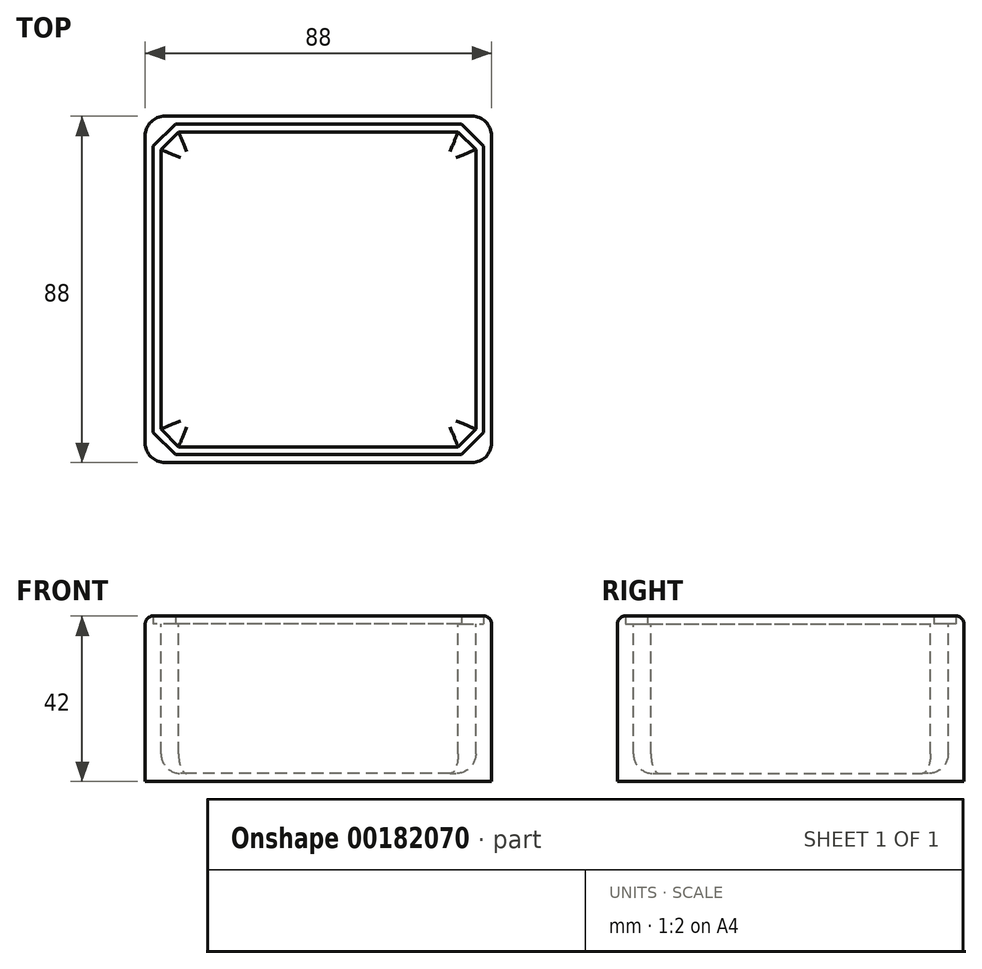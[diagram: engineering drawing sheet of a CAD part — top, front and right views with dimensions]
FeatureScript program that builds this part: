
annotation { "Feature Type Name" : "Feature", "Feature Type Description" : "" }
export const myFeature = defineFeature(function(context is Context, id is Id, definition is map)
    precondition{}
    {
        {
            var Q0;
            Q0=qCreatedBy(makeId("Top.planeOp"),FACE);
            var sketch = newSketch(context, id + "F0", { "sketchPlane" : qUnion([Q0])});
            skLineSegment(sketch, "E0.bottom", {"start": v(42, -42) * mm, "end": v(-42, -42) * mm});
            skLineSegment(sketch, "E0.top", {"start": v(42, 42) * mm, "end": v(-42, 42) * mm});
            skLineSegment(sketch, "E0.left", {"start": v(42, -42) * mm, "end": v(42, 42) * mm});
            skLineSegment(sketch, "E0.right", {"start": v(-42, -42) * mm, "end": v(-42, 42) * mm});
            skPoint(sketch, "E0.middle", {"position": v(0, 0) * mm});
            skLineSegment(sketch, "E1", {"start": v(-36.34, 42) * mm, "end": v(-42, 36.34) * mm});
            skLineSegment(sketch, "E2.MirrorCS", {"start": v(-36.34, -42) * mm, "end": v(-42, -36.34) * mm});
            skLineSegment(sketch, "E3.MirrorCS", {"start": v(36.34, 42) * mm, "end": v(42, 36.34) * mm});
            skLineSegment(sketch, "E4.MirrorCS", {"start": v(36.34, -42) * mm, "end": v(42, -36.34) * mm});
            skLineSegment(sketch, "E5.bottom", {"start": v(39, -44) * mm, "end": v(-39, -44) * mm});
            skLineSegment(sketch, "E5.top", {"start": v(39, 44) * mm, "end": v(-39, 44) * mm});
            skLineSegment(sketch, "E5.left", {"start": v(44, -39) * mm, "end": v(44, 39) * mm});
            skLineSegment(sketch, "E5.right", {"start": v(-44, -39) * mm, "end": v(-44, 39) * mm});
            skPoint(sketch, "E6.visualSharp", {"position": v(44, 44) * mm});
            skArc(sketch, "E6.filletArc", {"start": v(44, 39) * mm, "mid": v(42.54, 42.54) * mm, "end": v(39, 44) * mm});
            skPoint(sketch, "E7.visualSharp", {"position": v(-44, 44) * mm});
            skArc(sketch, "E7.filletArc", {"start": v(-39, 44) * mm, "mid": v(-42.54, 42.54) * mm, "end": v(-44, 39) * mm});
            skPoint(sketch, "E8.visualSharp", {"position": v(-44, -44) * mm});
            skArc(sketch, "E8.filletArc", {"start": v(-44, -39) * mm, "mid": v(-42.54, -42.54) * mm, "end": v(-39, -44) * mm});
            skPoint(sketch, "E9.visualSharp", {"position": v(44, -44) * mm});
            skArc(sketch, "E9.filletArc", {"start": v(39, -44) * mm, "mid": v(42.54, -42.54) * mm, "end": v(44, -39) * mm});
            skLineSegment(sketch, "E10.0", {"start": v(40, 40) * mm, "end": v(-40, 40) * mm});
            skLineSegment(sketch, "E10.1", {"start": v(40, -40) * mm, "end": v(40, 40) * mm});
            skLineSegment(sketch, "E10.2", {"start": v(40, -40) * mm, "end": v(-40, -40) * mm});
            skLineSegment(sketch, "E10.3", {"start": v(-40, -40) * mm, "end": v(-40, 40) * mm});
            skLineSegment(sketch, "E11.0", {"start": v(-35.51, 40) * mm, "end": v(-40, 35.51) * mm});
            skLineSegment(sketch, "E12.0", {"start": v(35.51, 40) * mm, "end": v(40, 35.51) * mm});
            skLineSegment(sketch, "E13.0", {"start": v(35.51, -40) * mm, "end": v(40, -35.51) * mm});
            skLineSegment(sketch, "E14.0", {"start": v(-35.51, -40) * mm, "end": v(-40, -35.51) * mm});
            skSolve(sketch);
        }
        {
            var Q0;
            Q0=makeQuery(id+"F0.imprint","IMPRINT",FACE,{"disambiguationData":[TD([[makeQuery(id+"F0.imprint","IMPRINT",EDGE,{"derivedFrom":sQuery(id+"F0.wireOp",EDGE,"E5.bottom")}),-1.0]])]});
            var Q1;
            {var subQ5=sQuery(id+"F0.wireOp",EDGE,"E11.0");Q1=makeQuery(id+"F0.imprint","IMPRINT",FACE,{"disambiguationData":[TD([[makeQuery(id+"F0.imprint","IMPRINT",EDGE,{"derivedFrom":subQ5}),1.0]])]});}
            var Q2;
            {var subQ5=sQuery(id+"F0.wireOp",EDGE,"E12.0");Q2=makeQuery(id+"F0.imprint","IMPRINT",FACE,{"disambiguationData":[TD([[makeQuery(id+"F0.imprint","IMPRINT",EDGE,{"derivedFrom":subQ5}),1.0]])]});}
            var Q3;
            {var subQ1=sQuery(id+"F0.wireOp",EDGE,"E0.left");var subQ5=sQuery(id+"F0.wireOp",EDGE,"E0.top");var subQ6=makeQuery(id+"F0.imprint","INTERSECT",VERTEX,{"derivedFrom":[subQ5,subQ1]});Q3=makeQuery(id+"F0.imprint","IMPRINT",FACE,{"disambiguationData":[TD([[makeQuery(id+"F0.imprint","IMPRINT",EDGE,{"disambiguationData":[TD([[subQ6,-1.0]])],"derivedFrom":subQ5}),1.0]])]});}
            var Q4;
            {var subQ0=sQuery(id+"F0.wireOp",EDGE,"E10.0");var subQ1=sQuery(id+"F0.wireOp",EDGE,"E3.MirrorCS");var subQ2=makeQuery(id+"F0.imprint","INTERSECT",VERTEX,{"derivedFrom":[subQ1,subQ0]});Q4=makeQuery(id+"F0.imprint","IMPRINT",FACE,{"disambiguationData":[TD([[makeQuery(id+"F0.imprint","IMPRINT",EDGE,{"disambiguationData":[TD([[subQ2,-1.0]])],"derivedFrom":subQ1}),1.0]])]});}
            var Q5;
            {var subQ4=sQuery(id+"F0.wireOp",EDGE,"E0.left");var subQ7=sQuery(id+"F0.wireOp",EDGE,"E3.MirrorCS");var subQ9=makeQuery(id+"F0.imprint","INTERSECT",VERTEX,{"derivedFrom":[subQ4,subQ7]});Q5=makeQuery(id+"F0.imprint","IMPRINT",FACE,{"disambiguationData":[TD([[makeQuery(id+"F0.imprint","IMPRINT",EDGE,{"disambiguationData":[TD([[subQ9,1.0]])],"derivedFrom":subQ4}),1.0]])]});}
            var Q6;
            {var subQ4=sQuery(id+"F0.wireOp",EDGE,"E0.top");var subQ6=sQuery(id+"F0.wireOp",EDGE,"E1");var subQ7=makeQuery(id+"F0.imprint","INTERSECT",VERTEX,{"derivedFrom":[subQ4,subQ6]});Q6=makeQuery(id+"F0.imprint","IMPRINT",FACE,{"disambiguationData":[TD([[makeQuery(id+"F0.imprint","IMPRINT",EDGE,{"disambiguationData":[TD([[subQ7,1.0]])],"derivedFrom":subQ4}),1.0]])]});}
            var Q7;
            {var subQ5=sQuery(id+"F0.wireOp",EDGE,"E11.0");Q7=makeQuery(id+"F0.imprint","IMPRINT",FACE,{"disambiguationData":[TD([[makeQuery(id+"F0.imprint","IMPRINT",EDGE,{"derivedFrom":subQ5}),-1.0]])]});}
            var Q8;
            {var subQ0=sQuery(id+"F0.wireOp",EDGE,"E10.0");var subQ1=sQuery(id+"F0.wireOp",EDGE,"E1");var subQ2=makeQuery(id+"F0.imprint","INTERSECT",VERTEX,{"derivedFrom":[subQ1,subQ0]});Q8=makeQuery(id+"F0.imprint","IMPRINT",FACE,{"disambiguationData":[TD([[makeQuery(id+"F0.imprint","IMPRINT",EDGE,{"disambiguationData":[TD([[subQ2,-1.0]])],"derivedFrom":subQ1}),-1.0]])]});}
            var Q9;
            {var subQ1=sQuery(id+"F0.wireOp",EDGE,"E0.right");var subQ5=sQuery(id+"F0.wireOp",EDGE,"E0.top");var subQ9=makeQuery(id+"F0.imprint","INTERSECT",VERTEX,{"derivedFrom":[subQ5,subQ1]});Q9=makeQuery(id+"F0.imprint","IMPRINT",FACE,{"disambiguationData":[TD([[makeQuery(id+"F0.imprint","IMPRINT",EDGE,{"disambiguationData":[TD([[subQ9,1.0]])],"derivedFrom":subQ5}),1.0]])]});}
            var Q10;
            {var subQ4=sQuery(id+"F0.wireOp",EDGE,"E0.right");var subQ6=sQuery(id+"F0.wireOp",EDGE,"E1");var subQ7=makeQuery(id+"F0.imprint","INTERSECT",VERTEX,{"derivedFrom":[subQ4,subQ6]});Q10=makeQuery(id+"F0.imprint","IMPRINT",FACE,{"disambiguationData":[TD([[makeQuery(id+"F0.imprint","IMPRINT",EDGE,{"disambiguationData":[TD([[subQ7,1.0]])],"derivedFrom":subQ4}),-1.0]])]});}
            var Q11;
            {var subQ5=sQuery(id+"F0.wireOp",EDGE,"E14.0");Q11=makeQuery(id+"F0.imprint","IMPRINT",FACE,{"disambiguationData":[TD([[makeQuery(id+"F0.imprint","IMPRINT",EDGE,{"derivedFrom":subQ5}),1.0]])]});}
            var Q12;
            {var subQ0=sQuery(id+"F0.wireOp",EDGE,"E10.2");var subQ1=sQuery(id+"F0.wireOp",EDGE,"E2.MirrorCS");var subQ2=makeQuery(id+"F0.imprint","INTERSECT",VERTEX,{"derivedFrom":[subQ1,subQ0]});Q12=makeQuery(id+"F0.imprint","IMPRINT",FACE,{"disambiguationData":[TD([[makeQuery(id+"F0.imprint","IMPRINT",EDGE,{"disambiguationData":[TD([[subQ2,-1.0]])],"derivedFrom":subQ1}),1.0]])]});}
            var Q13;
            {var subQ1=sQuery(id+"F0.wireOp",EDGE,"E0.bottom");var subQ5=sQuery(id+"F0.wireOp",EDGE,"E0.right");var subQ6=makeQuery(id+"F0.imprint","INTERSECT",VERTEX,{"derivedFrom":[subQ1,subQ5]});Q13=makeQuery(id+"F0.imprint","IMPRINT",FACE,{"disambiguationData":[TD([[makeQuery(id+"F0.imprint","IMPRINT",EDGE,{"disambiguationData":[TD([[subQ6,1.0]])],"derivedFrom":subQ1}),-1.0]])]});}
            var Q14;
            {var subQ1=sQuery(id+"F0.wireOp",EDGE,"E0.bottom");var subQ5=sQuery(id+"F0.wireOp",EDGE,"E2.MirrorCS");var subQ6=makeQuery(id+"F0.imprint","INTERSECT",VERTEX,{"derivedFrom":[subQ1,subQ5]});Q14=makeQuery(id+"F0.imprint","IMPRINT",FACE,{"disambiguationData":[TD([[makeQuery(id+"F0.imprint","IMPRINT",EDGE,{"disambiguationData":[TD([[subQ6,1.0]])],"derivedFrom":subQ1}),-1.0]])]});}
            var Q15;
            {var subQ5=sQuery(id+"F0.wireOp",EDGE,"E13.0");Q15=makeQuery(id+"F0.imprint","IMPRINT",FACE,{"disambiguationData":[TD([[makeQuery(id+"F0.imprint","IMPRINT",EDGE,{"derivedFrom":subQ5}),-1.0]])]});}
            var Q16;
            {var subQ0=sQuery(id+"F0.wireOp",EDGE,"E10.2");var subQ1=sQuery(id+"F0.wireOp",EDGE,"E4.MirrorCS");var subQ2=makeQuery(id+"F0.imprint","INTERSECT",VERTEX,{"derivedFrom":[subQ1,subQ0]});Q16=makeQuery(id+"F0.imprint","IMPRINT",FACE,{"disambiguationData":[TD([[makeQuery(id+"F0.imprint","IMPRINT",EDGE,{"disambiguationData":[TD([[subQ2,-1.0]])],"derivedFrom":subQ1}),-1.0]])]});}
            var Q17;
            {var subQ1=sQuery(id+"F0.wireOp",EDGE,"E0.bottom");var subQ5=sQuery(id+"F0.wireOp",EDGE,"E0.left");var subQ6=makeQuery(id+"F0.imprint","INTERSECT",VERTEX,{"derivedFrom":[subQ1,subQ5]});Q17=makeQuery(id+"F0.imprint","IMPRINT",FACE,{"disambiguationData":[TD([[makeQuery(id+"F0.imprint","IMPRINT",EDGE,{"disambiguationData":[TD([[subQ6,-1.0]])],"derivedFrom":subQ1}),-1.0]])]});}
            extrude(context, id + "F1", {"entities" : qUnion([Q0, Q1, Q2, Q3, Q4, Q5, Q6, Q7, Q8, Q9, Q10, Q11, Q12, Q13, Q14, Q15, Q16, Q17]), "oppositeDirection" : true, "depth" : 40 * mm});
        }
        {
            var Q0;
            {var subQ5=sQuery(id+"F0.wireOp",EDGE,"E11.0");Q0=makeQuery(id+"F0.imprint","IMPRINT",FACE,{"disambiguationData":[TD([[makeQuery(id+"F0.imprint","IMPRINT",EDGE,{"derivedFrom":subQ5}),1.0]])]});}
            extrude(context, id + "F2", {"entities" : qUnion([Q0]), "operationType" : NewBodyOperationType.REMOVE, "oppositeDirection" : true, "depth" : 38 * mm});
        }
        {
            var Q0;
            Q0=makeQuery(id+"F0.imprint","IMPRINT",FACE,{"disambiguationData":[TD([[makeQuery(id+"F0.imprint","IMPRINT",EDGE,{"derivedFrom":sQuery(id+"F0.wireOp",EDGE,"E5.bottom")}),-1.0]])]});
            var Q1;
            {var subQ1=sQuery(id+"F0.wireOp",EDGE,"E0.right");var subQ5=sQuery(id+"F0.wireOp",EDGE,"E0.top");var subQ9=makeQuery(id+"F0.imprint","INTERSECT",VERTEX,{"derivedFrom":[subQ5,subQ1]});Q1=makeQuery(id+"F0.imprint","IMPRINT",FACE,{"disambiguationData":[TD([[makeQuery(id+"F0.imprint","IMPRINT",EDGE,{"disambiguationData":[TD([[subQ9,1.0]])],"derivedFrom":subQ5}),1.0]])]});}
            var Q2;
            {var subQ0=sQuery(id+"F0.wireOp",EDGE,"E10.0");var subQ1=sQuery(id+"F0.wireOp",EDGE,"E1");var subQ2=makeQuery(id+"F0.imprint","INTERSECT",VERTEX,{"derivedFrom":[subQ1,subQ0]});Q2=makeQuery(id+"F0.imprint","IMPRINT",FACE,{"disambiguationData":[TD([[makeQuery(id+"F0.imprint","IMPRINT",EDGE,{"disambiguationData":[TD([[subQ2,-1.0]])],"derivedFrom":subQ1}),-1.0]])]});}
            var Q3;
            {var subQ1=sQuery(id+"F0.wireOp",EDGE,"E0.left");var subQ5=sQuery(id+"F0.wireOp",EDGE,"E0.top");var subQ6=makeQuery(id+"F0.imprint","INTERSECT",VERTEX,{"derivedFrom":[subQ5,subQ1]});Q3=makeQuery(id+"F0.imprint","IMPRINT",FACE,{"disambiguationData":[TD([[makeQuery(id+"F0.imprint","IMPRINT",EDGE,{"disambiguationData":[TD([[subQ6,-1.0]])],"derivedFrom":subQ5}),1.0]])]});}
            var Q4;
            {var subQ0=sQuery(id+"F0.wireOp",EDGE,"E10.0");var subQ1=sQuery(id+"F0.wireOp",EDGE,"E3.MirrorCS");var subQ2=makeQuery(id+"F0.imprint","INTERSECT",VERTEX,{"derivedFrom":[subQ1,subQ0]});Q4=makeQuery(id+"F0.imprint","IMPRINT",FACE,{"disambiguationData":[TD([[makeQuery(id+"F0.imprint","IMPRINT",EDGE,{"disambiguationData":[TD([[subQ2,-1.0]])],"derivedFrom":subQ1}),1.0]])]});}
            var Q5;
            {var subQ1=sQuery(id+"F0.wireOp",EDGE,"E0.bottom");var subQ5=sQuery(id+"F0.wireOp",EDGE,"E0.left");var subQ6=makeQuery(id+"F0.imprint","INTERSECT",VERTEX,{"derivedFrom":[subQ1,subQ5]});Q5=makeQuery(id+"F0.imprint","IMPRINT",FACE,{"disambiguationData":[TD([[makeQuery(id+"F0.imprint","IMPRINT",EDGE,{"disambiguationData":[TD([[subQ6,-1.0]])],"derivedFrom":subQ1}),-1.0]])]});}
            var Q6;
            {var subQ0=sQuery(id+"F0.wireOp",EDGE,"E10.2");var subQ1=sQuery(id+"F0.wireOp",EDGE,"E4.MirrorCS");var subQ2=makeQuery(id+"F0.imprint","INTERSECT",VERTEX,{"derivedFrom":[subQ1,subQ0]});Q6=makeQuery(id+"F0.imprint","IMPRINT",FACE,{"disambiguationData":[TD([[makeQuery(id+"F0.imprint","IMPRINT",EDGE,{"disambiguationData":[TD([[subQ2,-1.0]])],"derivedFrom":subQ1}),-1.0]])]});}
            var Q7;
            {var subQ1=sQuery(id+"F0.wireOp",EDGE,"E0.bottom");var subQ5=sQuery(id+"F0.wireOp",EDGE,"E0.right");var subQ6=makeQuery(id+"F0.imprint","INTERSECT",VERTEX,{"derivedFrom":[subQ1,subQ5]});Q7=makeQuery(id+"F0.imprint","IMPRINT",FACE,{"disambiguationData":[TD([[makeQuery(id+"F0.imprint","IMPRINT",EDGE,{"disambiguationData":[TD([[subQ6,1.0]])],"derivedFrom":subQ1}),-1.0]])]});}
            var Q8;
            {var subQ0=sQuery(id+"F0.wireOp",EDGE,"E10.2");var subQ1=sQuery(id+"F0.wireOp",EDGE,"E2.MirrorCS");var subQ2=makeQuery(id+"F0.imprint","INTERSECT",VERTEX,{"derivedFrom":[subQ1,subQ0]});Q8=makeQuery(id+"F0.imprint","IMPRINT",FACE,{"disambiguationData":[TD([[makeQuery(id+"F0.imprint","IMPRINT",EDGE,{"disambiguationData":[TD([[subQ2,-1.0]])],"derivedFrom":subQ1}),1.0]])]});}
            extrude(context, id + "F3", {"entities" : qUnion([Q0, Q1, Q2, Q3, Q4, Q5, Q6, Q7, Q8]), "operationType" : NewBodyOperationType.ADD, "depth" : 2 * mm});
        }
        {
            var Q0;
            Q0=makeQuery(id+"F3.opExtrude","CAP_EDGE",EDGE,{"disambiguationData":[OSD([sQuery(id+"F0.wireOp",EDGE,"E8.filletArc")])],"isStart":false});
            fillet(context, id + "F4", {"entities" : qUnion([Q0]), "radius" : 2 * mm, "tangentPropagation" : true, "allowEdgeOverflow" : false});
        }
        {
            var Q0;
            Q0=makeQuery(id+"F2.boolean.opBoolean","COPY",EDGE,{"derivedFrom":makeQuery(id+"F2.opExtrude","CAP_EDGE",EDGE,{"disambiguationData":[OSD([sQuery(id+"F0.wireOp",EDGE,"E10.0")])],"isStart":false})});
            var Q1;
            Q1=makeQuery(id+"F2.boolean.opBoolean","COPY",EDGE,{"derivedFrom":makeQuery(id+"F2.opExtrude","CAP_EDGE",EDGE,{"disambiguationData":[OSD([sQuery(id+"F0.wireOp",EDGE,"E10.3")])],"isStart":false})});
            var Q2;
            Q2=makeQuery(id+"F2.boolean.opBoolean","COPY",EDGE,{"derivedFrom":makeQuery(id+"F2.opExtrude","CAP_EDGE",EDGE,{"disambiguationData":[OSD([sQuery(id+"F0.wireOp",EDGE,"E11.0")])],"isStart":false})});
            var Q3;
            Q3=makeQuery(id+"F2.boolean.opBoolean","COPY",EDGE,{"derivedFrom":makeQuery(id+"F2.opExtrude","CAP_EDGE",EDGE,{"disambiguationData":[OSD([sQuery(id+"F0.wireOp",EDGE,"E14.0")])],"isStart":false})});
            var Q4;
            Q4=makeQuery(id+"F2.boolean.opBoolean","COPY",EDGE,{"derivedFrom":makeQuery(id+"F2.opExtrude","CAP_EDGE",EDGE,{"disambiguationData":[OSD([sQuery(id+"F0.wireOp",EDGE,"E10.2")])],"isStart":false})});
            var Q5;
            Q5=makeQuery(id+"F2.boolean.opBoolean","COPY",EDGE,{"derivedFrom":makeQuery(id+"F2.opExtrude","CAP_EDGE",EDGE,{"disambiguationData":[OSD([sQuery(id+"F0.wireOp",EDGE,"E13.0")])],"isStart":false})});
            var Q6;
            Q6=makeQuery(id+"F2.boolean.opBoolean","COPY",EDGE,{"derivedFrom":makeQuery(id+"F2.opExtrude","CAP_EDGE",EDGE,{"disambiguationData":[OSD([sQuery(id+"F0.wireOp",EDGE,"E10.1")])],"isStart":false})});
            var Q7;
            Q7=makeQuery(id+"F2.boolean.opBoolean","COPY",EDGE,{"derivedFrom":makeQuery(id+"F2.opExtrude","CAP_EDGE",EDGE,{"disambiguationData":[OSD([sQuery(id+"F0.wireOp",EDGE,"E12.0")])],"isStart":false})});
            fillet(context, id + "F5", {"entities" : qUnion([Q0, Q1, Q2, Q3, Q4, Q5, Q6, Q7]), "radius" : 5 * mm, "tangentPropagation" : true, "allowEdgeOverflow" : false});
        }
    });
